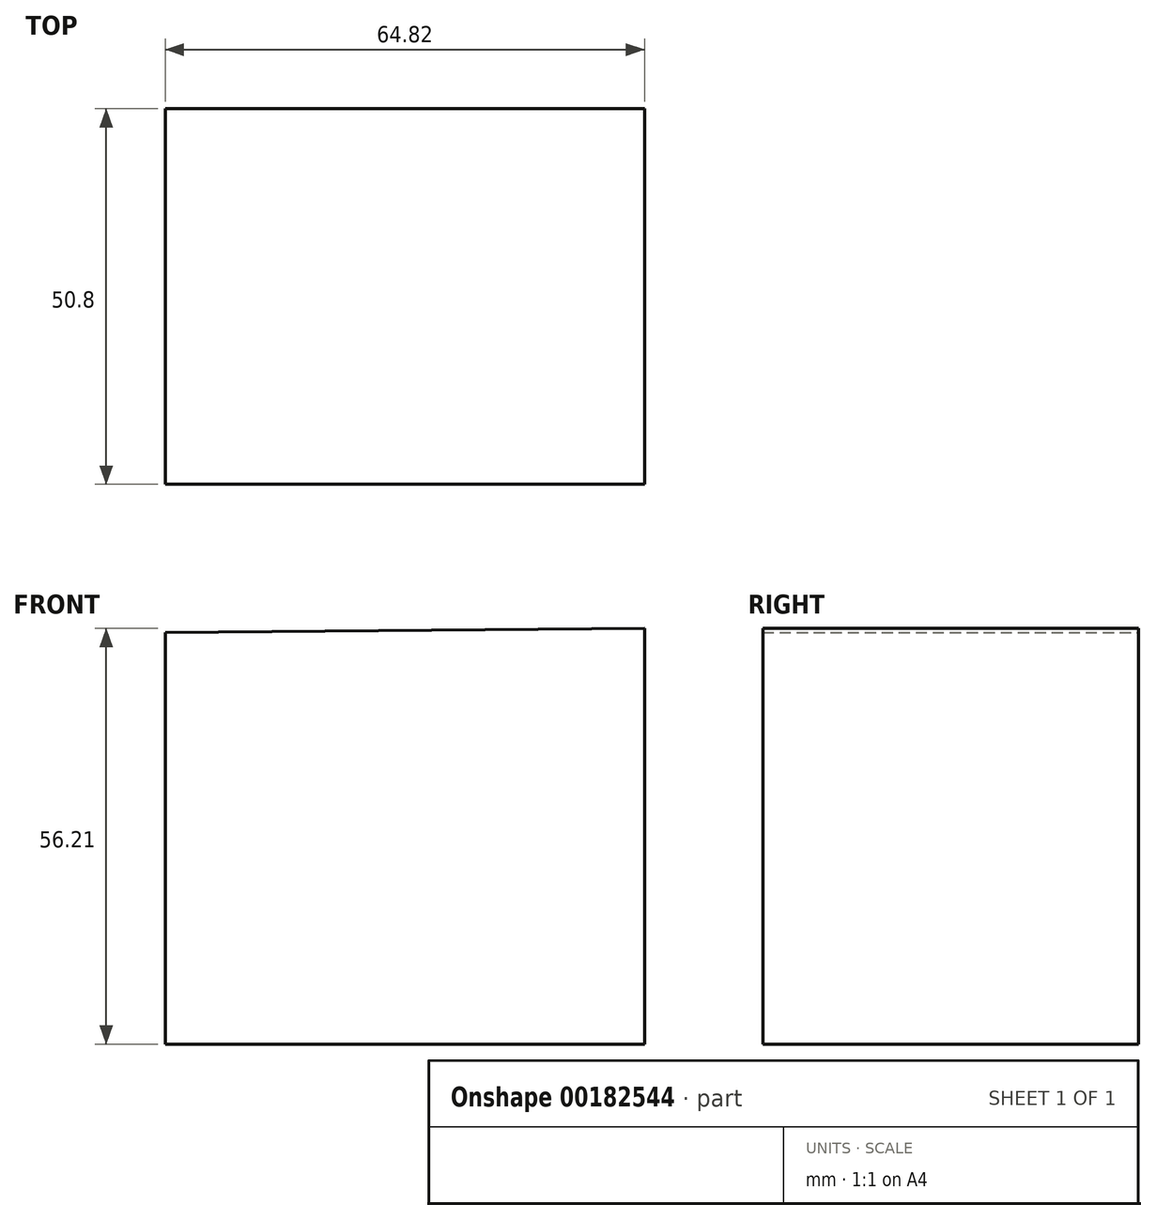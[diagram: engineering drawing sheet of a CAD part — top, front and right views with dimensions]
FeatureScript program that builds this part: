
annotation { "Feature Type Name" : "Feature", "Feature Type Description" : "" }
export const myFeature = defineFeature(function(context is Context, id is Id, definition is map)
    precondition{}
    {
        {
            var Q0;
            Q0=qCreatedBy(makeId("Front.planeOp"),FACE);
            var sketch = newSketch(context, id + "F0", { "sketchPlane" : qUnion([Q0])});
            skCircle(sketch, "E0", {"center": v(0, 0) * mm, "radius": 8.57 * mm});
            skLineSegment(sketch, "E1", {"start": v(-39.5, 35.73) * mm, "end": v(-39.5, -37.22) * mm});
            skLineSegment(sketch, "E2", {"start": v(-39.5, -37.22) * mm, "end": v(39.5, -37.22) * mm});
            skLineSegment(sketch, "E3", {"start": v(39.5, -37.22) * mm, "end": v(39.5, 36.23) * mm});
            skLineSegment(sketch, "E4", {"start": v(-39.5, 35.73) * mm, "end": v(39.5, 36.23) * mm});
            skSolve(sketch);
        }
        {
            var Q0;
            Q0=makeQuery(id+"F0.imprint","IMPRINT",FACE,{"disambiguationData":[TD([[makeQuery(id+"F0.imprint","IMPRINT",EDGE,{"derivedFrom":sQuery(id+"F0.wireOp",EDGE,"E0")}),1.0]])]});
            extrude(context, id + "F1", {"entities" : qUnion([Q0]), "depth" : 25.4 * mm});
        }
        {
            var Q0;
            Q0=qCreatedBy(makeId("Front.planeOp"),FACE);
            var sketch = newSketch(context, id + "F2", { "sketchPlane" : qUnion([Q0])});
            skLineSegment(sketch, "E5", {"start": v(-31.9, 26.07) * mm, "end": v(-31.9, -29.62) * mm});
            skLineSegment(sketch, "E6", {"start": v(-31.9, -29.62) * mm, "end": v(32.92, -29.62) * mm});
            skLineSegment(sketch, "E7", {"start": v(32.92, -29.62) * mm, "end": v(32.92, 26.59) * mm});
            skLineSegment(sketch, "E8", {"start": v(-31.9, 26.07) * mm, "end": v(32.92, 26.59) * mm});
            skSolve(sketch);
        }
        {
            var Q0;
            Q0=makeQuery(id+"F2.imprint","IMPRINT",FACE,{"disambiguationData":[TD([[makeQuery(id+"F2.imprint","IMPRINT",EDGE,{"derivedFrom":sQuery(id+"F2.wireOp",EDGE,"E5")}),1.0]])]});
            extrude(context, id + "F3", {"entities" : qUnion([Q0]), "operationType" : NewBodyOperationType.ADD, "depth" : 50.8 * mm});
        }
    });
